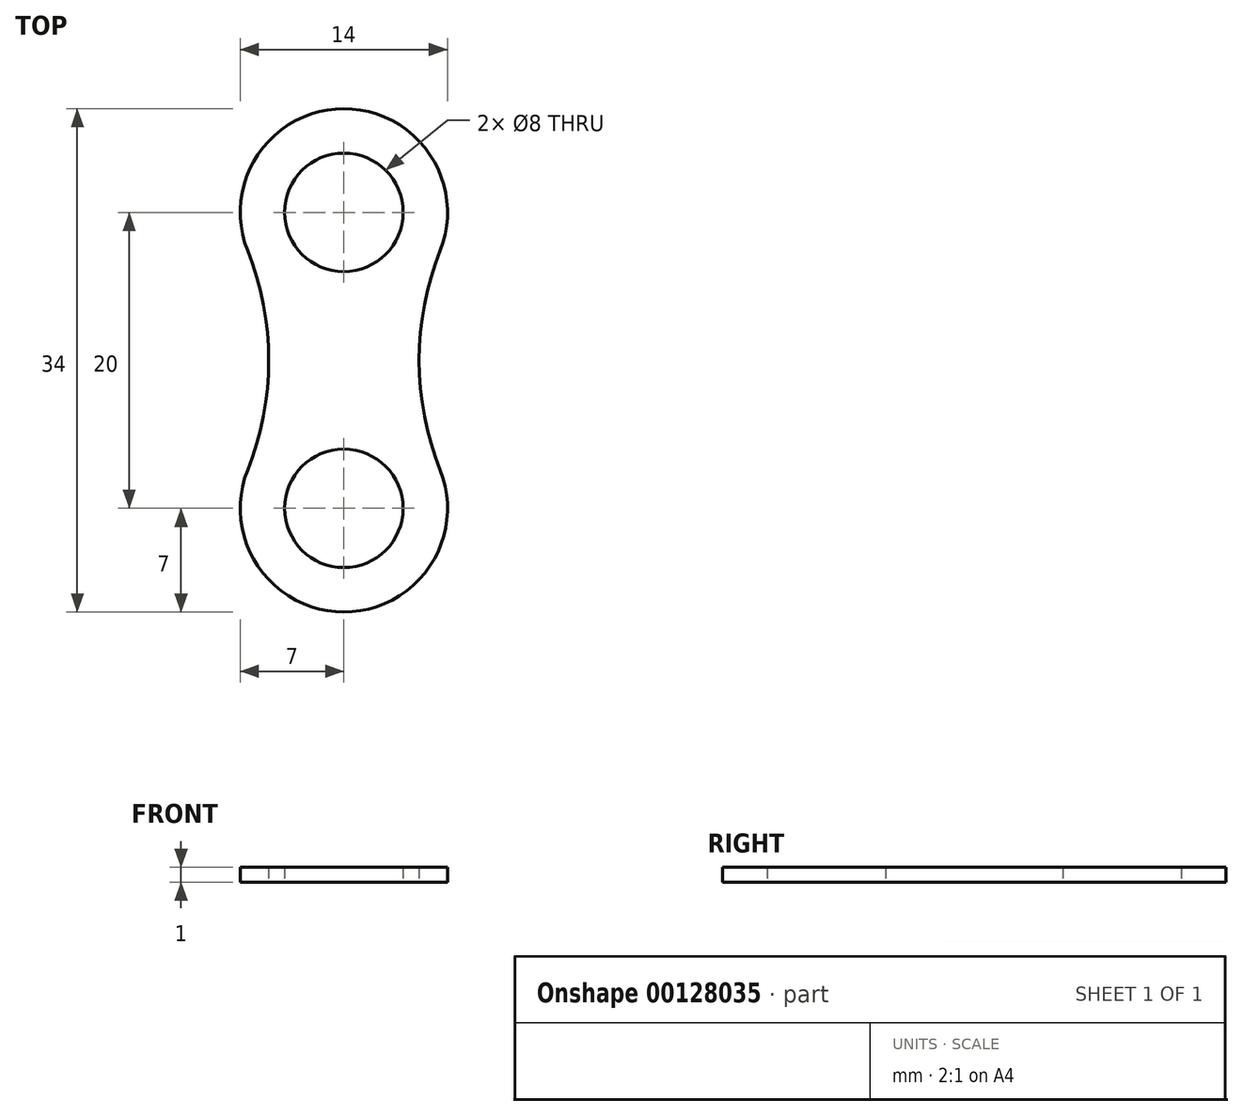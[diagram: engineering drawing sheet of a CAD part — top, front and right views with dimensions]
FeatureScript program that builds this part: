
annotation { "Feature Type Name" : "Feature", "Feature Type Description" : "" }
export const myFeature = defineFeature(function(context is Context, id is Id, definition is map)
    precondition{}
    {
        {
            var Q0;
            Q0=qCreatedBy(makeId("Top.planeOp"),FACE);
            var sketch = newSketch(context, id + "F0", { "sketchPlane" : qUnion([Q0])});
            skArc(sketch, "E0", {"start": v(6.5, 7.4) * mm, "mid": v(0, 17) * mm, "end": v(-6.5, 7.4) * mm});
            skArc(sketch, "E1", {"start": v(-6.5, -7.4) * mm, "mid": v(0, -17) * mm, "end": v(6.5, -7.4) * mm});
            skArc(sketch, "E2", {"start": v(-6.5, -7.4) * mm, "mid": v(-5.08, 0) * mm, "end": v(-6.5, 7.4) * mm});
            skArc(sketch, "E3", {"start": v(6.5, 7.4) * mm, "mid": v(5.08, 0) * mm, "end": v(6.5, -7.4) * mm});
            skCircle(sketch, "E4", {"center": v(0, 10) * mm, "radius": 4 * mm});
            skCircle(sketch, "E5", {"center": v(0, -10) * mm, "radius": 4 * mm});
            skSolve(sketch);
        }
        {
            var Q0;
            Q0 = qSketchRegion(id + "F0", true);
            extrude(context, id + "F1", {"entities" : qUnion([Q0]), "depth" : 1 * mm});
        }
    });
